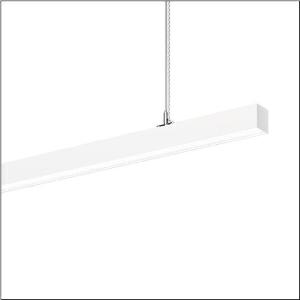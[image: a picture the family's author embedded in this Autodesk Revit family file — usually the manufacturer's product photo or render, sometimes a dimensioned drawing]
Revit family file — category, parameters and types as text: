
# Revit family: silica_r__21_51mx30tbt5w_3ed0
name_source: partatom
category: Lighting Fixtures
units: mm (PartAtom-declared; Revit-internal decimal feet)

## family parameters
Cut with Voids When Loaded = No
Host = Face
Light Source = No
Part Type = Normal
Room Calculation Point = No
Round Connector Dimension = Use Diameter
Shared = No

## types (1)
- --- (1 x LED, 5150 lm, 42.2 W, 6500K)
    Apparent Load = 42 VA
    CIE Flux Codes = 47 79 96 58 100
    Color Rendering = 80
    Color Temperature = 6500K
    Default Elevation = 1800 mm
    Description = Silica® 21, office luminaire, primary optical cover: cover, of PMMA, opal, light emission: direct/indirect distribution, primary light characteristic: symmetric, installation type: suspended mounting, LED, rated luminous flux: 5.150lm, luminous efficacy: 116lm/W, light colour: 8tw, colour temperature: 2700..6500K, control gear: ECG DALI, with terminal, 3+2-pole, max. 2.5mm², mains connection: 220..240V, AC, 50/60Hz, rated input power: 44.3W, luminaire housing, of aluminium, traffic white (RAL 9016), length: 1.504mm, width: 53mm, height: 53mm, protection rating (complete): IP20, insulation class (complete): insulation class I (protective earthing), certification: CE, permissible operating ambient temperature: 0..+35°C, standard: EN 50419, packaging unit: 1 piece
    Height = 53 mm
    Lamp = 1 x LED
    Lamp Light Flux = 5150 lm
    Lamp Power = 42.2 W
    Lamp count = 1
    Length = 1504 mm
    Luminous efficacy = 122 lm/W
    Manufacturer = Siteco
    ModVariant = No
    Model = 51MX30TBT5W
    Mounting Place = Ceiling
    Mounting Type = Pendant
    Number of Poles = 1
    OnlyDefault = Yes
    Power Factor = 1
    Product Name = Silica® 21
    Product group = office luminaire | ceiling pendant
    ProductGroupID = 902
    Protection Class = Protection class I
    Protection Degree = IP 20
    RLX_Detail_Level = 1
    RLX_Emergency_Light_Flux = 0 lm
    RLX_Emergency_Type = 0
    RLX_Emergency_Type_DB = No
    RlxData = <blob elided: 18213 chars, md5=c9798cba>
    Socket = socket
    Standby Power = 0 W
    System Light Flux = 5150 lm
    System Power = 42 W
    Type Comments = individual setting
    Type Image = l_1313629.jpg
    URL = http://relux.com
    VarID = @adj_089019
    Voltage = 0 V
    Weight = 0.00 kg
    Width = 53 mm

## geometry (parser evidence)
native form markers: Blend x4, Sweep x12
no freeform markers — native parametric forms only
